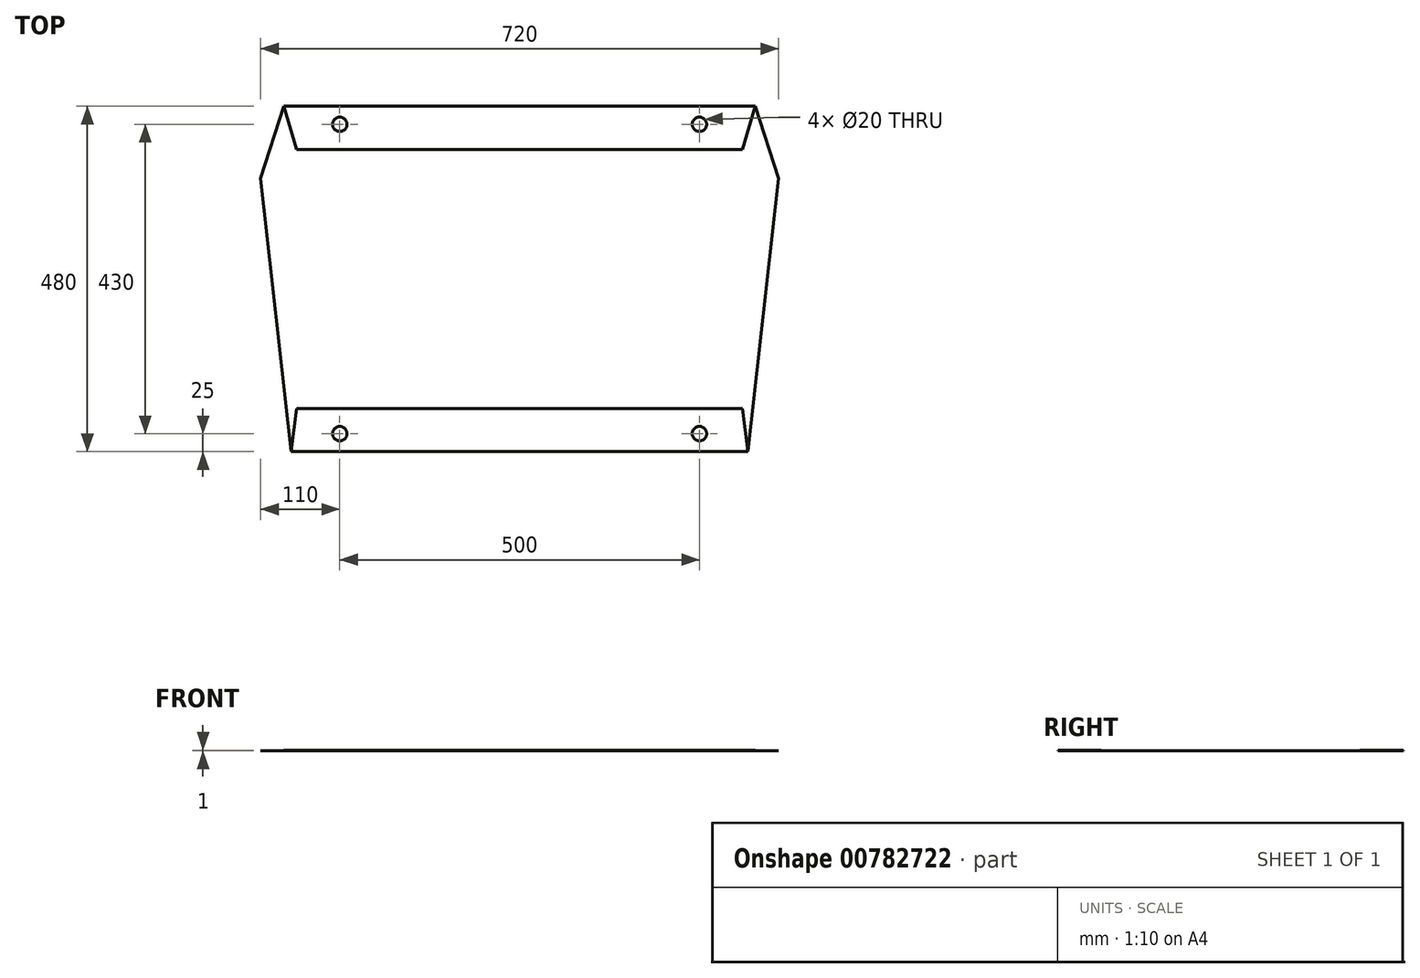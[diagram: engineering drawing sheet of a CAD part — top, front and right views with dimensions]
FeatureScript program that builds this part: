
annotation { "Feature Type Name" : "Feature", "Feature Type Description" : "" }
export const myFeature = defineFeature(function(context is Context, id is Id, definition is map)
    precondition{}
    {
        {
            var Q0;
            Q0=qCreatedBy(makeId("Top.planeOp"),FACE);
            var sketch = newSketch(context, id + "F0", { "sketchPlane" : qUnion([Q0])});
            skLineSegment(sketch, "E0", {"start": v(-655, 0) * mm, "end": v(0, 0) * mm});
            skLineSegment(sketch, "E1", {"start": v(0, 0) * mm, "end": v(32.5, -100) * mm});
            skLineSegment(sketch, "E2", {"start": v(32.5, -100) * mm, "end": v(-10, -480) * mm});
            skLineSegment(sketch, "E3", {"start": v(-10, -480) * mm, "end": v(-645, -480) * mm});
            skLineSegment(sketch, "E4", {"start": v(-645, -480) * mm, "end": v(-687.5, -100) * mm});
            skLineSegment(sketch, "E5", {"start": v(-687.5, -100) * mm, "end": v(-655, 0) * mm});
            skSolve(sketch);
        }
        {
            var Q0;
            Q0=qSketchRegion(id+"F0",true);
            extrude(context, id + "F1", {"entities" : qUnion([Q0]), "depth" : .5 * mm, "offsetDistance" : 25 * mm});
        }
        {
            var Q0;
            Q0=makeQuery(id+"F1.opExtrude","CAP_FACE",FACE,{"disambiguationData":[OSD([sQuery(id+"F0.wireOp",EDGE,"E0"),sQuery(id+"F0.wireOp",EDGE,"E1"),sQuery(id+"F0.wireOp",EDGE,"E2"),sQuery(id+"F0.wireOp",EDGE,"E3"),sQuery(id+"F0.wireOp",EDGE,"E4"),sQuery(id+"F0.wireOp",EDGE,"E5")])],"isStart":false});
            var sketch = newSketch(context, id + "F2", { "sketchPlane" : qUnion([Q0])});
            skLineSegment(sketch, "E6", {"start": v(-655, 0) * mm, "end": v(-637.5, -60) * mm});
            skLineSegment(sketch, "E7", {"start": v(-637.5, -60) * mm, "end": v(-17.5, -60) * mm});
            skLineSegment(sketch, "E8", {"start": v(-17.5, -60) * mm, "end": v(0, 0) * mm});
            skLineSegment(sketch, "E9", {"start": v(0, 0) * mm, "end": v(-655, 0) * mm});
            skLineSegment(sketch, "E10.0", {"start": v(-10, -480) * mm, "end": v(-645, -480) * mm});
            skLineSegment(sketch, "E11", {"start": v(-645, -480) * mm, "end": v(-637.5, -420) * mm});
            skLineSegment(sketch, "E12", {"start": v(-637.5, -420) * mm, "end": v(-17.5, -420) * mm});
            skLineSegment(sketch, "E13", {"start": v(-17.5, -420) * mm, "end": v(-10, -480) * mm});
            skSolve(sketch);
        }
        {
            var Q0;
            Q0=qSketchRegion(id+"F2",true);
            extrude(context, id + "F3", {"entities" : qUnion([Q0]), "operationType" : NewBodyOperationType.ADD, "depth" : .5 * mm, "offsetDistance" : 25 * mm});
        }
        {
            var Q0;
            Q0=makeQuery(id+"F3.opExtrude","CAP_FACE",FACE,{"disambiguationData":[OSD([sQuery(id+"F2.wireOp",EDGE,"E6"),sQuery(id+"F2.wireOp",EDGE,"E7"),sQuery(id+"F2.wireOp",EDGE,"E8"),sQuery(id+"F2.wireOp",EDGE,"E9")])],"isStart":false});
            var sketch = newSketch(context, id + "F4", { "sketchPlane" : qUnion([Q0])});
            skCircle(sketch, "E14", {"center": v(-577.5, -25) * mm, "radius": 10 * mm});
            skCircle(sketch, "E15.0.1.0", {"center": v(-577.5, -455) * mm, "radius": 10 * mm});
            skCircle(sketch, "E15.1.0.0", {"center": v(-77.5, -25) * mm, "radius": 10 * mm});
            skCircle(sketch, "E15.1.1.0", {"center": v(-77.5, -455) * mm, "radius": 10 * mm});
            skLineSegment(sketch, "E15.direction1", {"start": v(-577.5, -25) * mm, "end": v(-77.5, -25) * mm, "construction": true});
            skLineSegment(sketch, "E15.direction2", {"start": v(-577.5, -25) * mm, "end": v(-577.5, -455) * mm, "construction": true});
            skSolve(sketch);
        }
        {
            var Q0;
            Q0 = qSketchRegion(id + "F4", true);
            var Q1;
            Q1 = qConstructionFilter(qBodyType(qCreatedBy(id + "F4" ,EDGE), BodyType.WIRE), ConstructionObject.NO);
            extrude(context, id + "F5", {"entities" : qUnion([Q0]), "operationType" : NewBodyOperationType.REMOVE, "surfaceEntities" : qUnion([Q1]), "oppositeDirection" : true, "depth" : 25 * mm, "offsetDistance" : 25 * mm});
        }
    });
